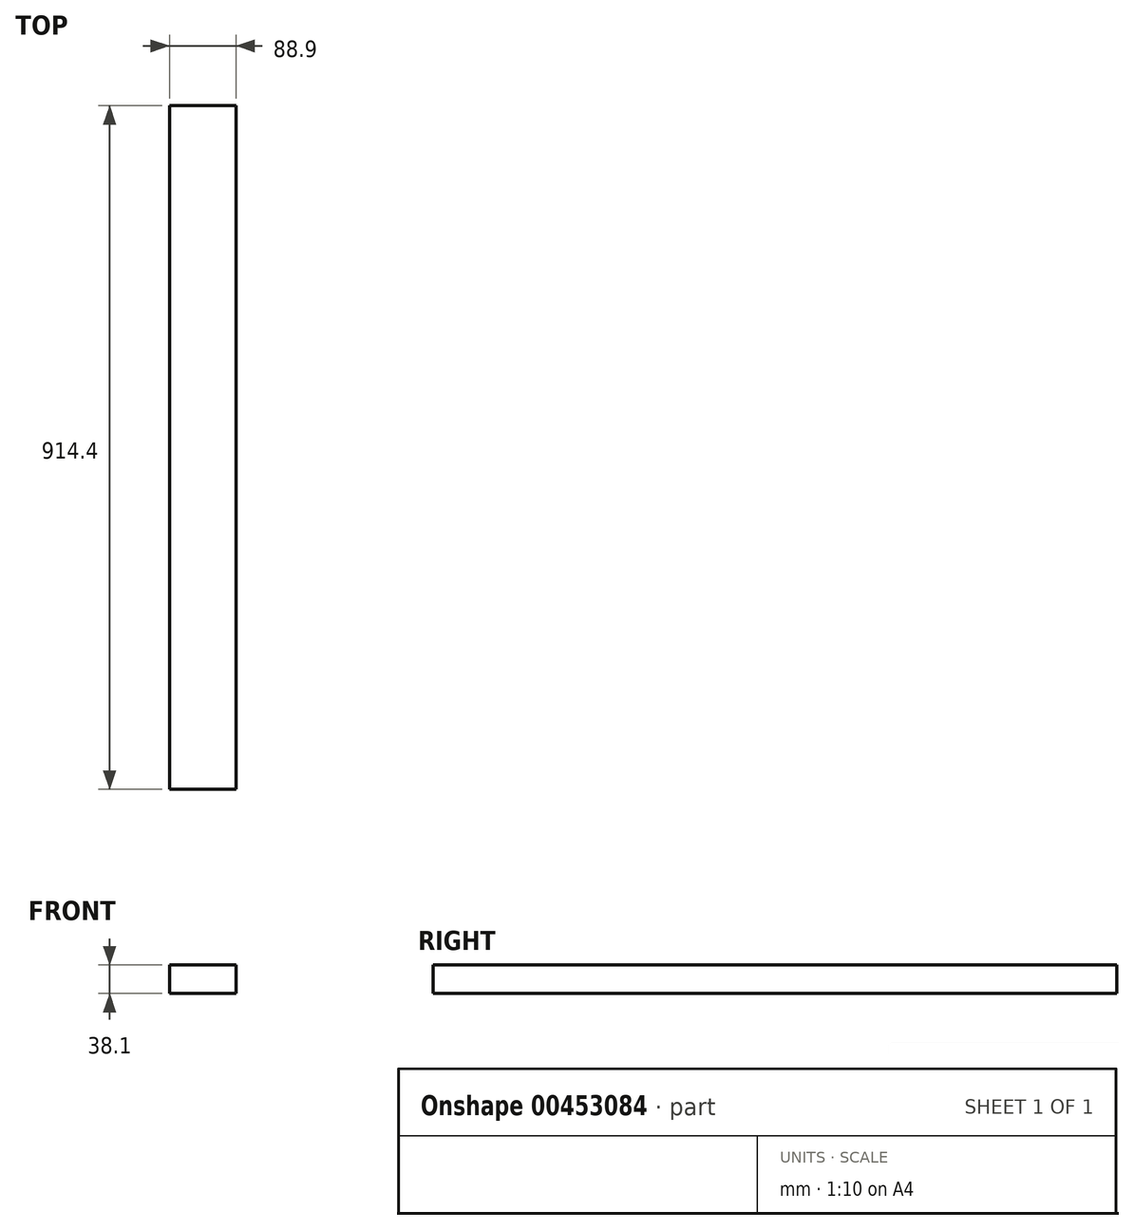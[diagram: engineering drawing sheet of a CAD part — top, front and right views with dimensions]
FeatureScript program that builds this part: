
annotation { "Feature Type Name" : "Feature", "Feature Type Description" : "" }
export const myFeature = defineFeature(function(context is Context, id is Id, definition is map)
    precondition{}
    {
        {
            var Q0;
            Q0=qCreatedBy(makeId("Front.planeOp"),FACE);
            var sketch = newSketch(context, id + "F0", { "sketchPlane" : qUnion([Q0])});
            skLineSegment(sketch, "E0.bottom", {"start": v(44.45, 19.05) * mm, "end": v(-44.45, 19.05) * mm});
            skLineSegment(sketch, "E0.top", {"start": v(44.45, -19.05) * mm, "end": v(-44.45, -19.05) * mm});
            skLineSegment(sketch, "E0.left", {"start": v(44.45, 19.05) * mm, "end": v(44.45, -19.05) * mm});
            skLineSegment(sketch, "E0.right", {"start": v(-44.45, 19.05) * mm, "end": v(-44.45, -19.05) * mm});
            skPoint(sketch, "E0.middle", {"position": v(0, 0) * mm});
            skSolve(sketch);
        }
        {
            var Q0;
            Q0 = qSketchRegion(id + "F0", true);
            extrude(context, id + "F1", {"entities" : qUnion([Q0]), "depth" : 914.4 * mm, "offsetDistance" : 25.4 * mm});
        }
    });
